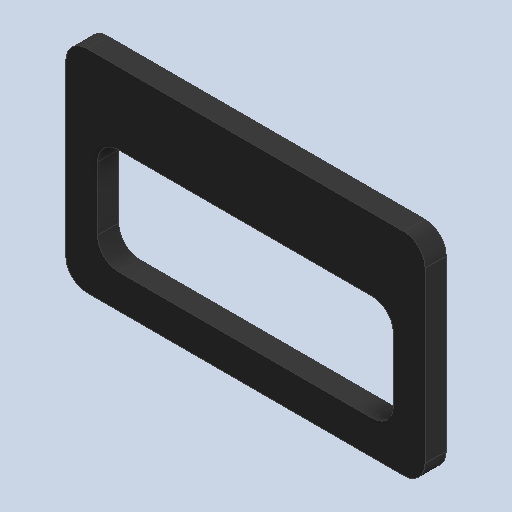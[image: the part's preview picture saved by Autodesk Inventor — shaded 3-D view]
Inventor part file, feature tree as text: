
AUTODESK INVENTOR PART (.ipt)
format: ipt  version: 2024.2 (Build 282272000, 272)  size: 126,464 bytes
history: native  units: mm
features: fillet x2, extrude x1
ambient origin geometry x8: Origin, YZ Plane, XZ Plane, XY Plane, X Axis, Y Axis, Z Axis, Center Point
bodies: Solid1 (feature_tree)
feature tree (3):
  extrude  "Extrusion1"  Depth=10.0mm
  fillet  "Fillet1"  Radius=17.0mm
  fillet  "Fillet2"  Radius=4.1mm
